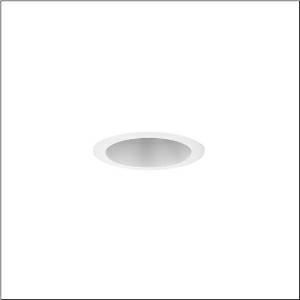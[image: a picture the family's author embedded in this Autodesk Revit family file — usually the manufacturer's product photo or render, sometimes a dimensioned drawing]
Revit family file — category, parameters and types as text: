
# Revit family: lunis_31-l_51dn15ee31b
name_source: partatom
category: Lighting Fixtures
units: mm (PartAtom-declared; Revit-internal decimal feet)

## family parameters
Cut with Voids When Loaded = No
Host = Face
Light Source = No
Part Type = Normal
Room Calculation Point = No
Round Connector Dimension = Use Diameter
Shared = No

## types (1)
- --- (1 x LED, 1650 lm, 12.2 W, 3000K)
    Apparent Load = 12 VA
    CIE Flux Codes = 93 98 100 100 100
    Color Rendering = 80
    Color Temperature = 3000K
    Default Elevation = 1800 mm
    Description = Lunis 31, -L, downlight, light control with reflector, light emission: direct distribution, LED rated luminous flux: 1.650lm, light colour: 830, mains connection: 220..240V, AC, 50/60Hz, housing, of aluminium, white, protection rating (complete): IP20, protection rating (on room side): IP54, insulation class (complete): insulation class II (safety insulation), certification: CE, packaging unit: 1 piece
    Height = 0 mm  [stored 0 ft]
    Lamp = 1 x LED
    Lamp Light Flux = 1650 lm
    Lamp Power = 12.2 W
    Lamp count = 1
    Length = 188 mm  [stored 0.616798 ft]
    Luminous efficacy = 135 lm/W
    Manufacturer = Siteco
    ModVariant = No
    Model = 51DN15EE31B
    Mounting Place = Ceiling
    Mounting Type = Recessed
    Number of Poles = 1
    OnlyDefault = Yes
    Power Factor = 1
    Product Name = Lunis 31-L
    Product group = downlight
    ProductGroupID = 400
    Protection Class = Protection class II
    Protection Degree = IP 20
    RLX_Detail_Level = 1
    RLX_Emergency_Light_Flux = 0 lm
    RLX_Emergency_Type = 0
    RLX_Emergency_Type_DB = No
    RlxData = <blob elided: 22105 chars, md5=31a4c4ed>
    Socket = socket
    Standby Power = 0 W
    System Light Flux = 1650 lm
    System Power = 12 W
    Type Comments = individual setting: luminous flux: 100 % | (OFF | ON) | 300 mA
    Type Image = l_1345911.jpg
    URL = http://relux.com
    VarID = @adj_010131
    Voltage = 0 V
    Weight = 0.00 kg
    Width = 0 mm  [stored 0 ft]

note: [stored X ft] marks values corroborated as IEEE doubles in the binary element streams (Revit-internal decimal feet)

## geometry (parser evidence)
native form markers: Blend x4, Sweep x14
no freeform markers — native parametric forms only
